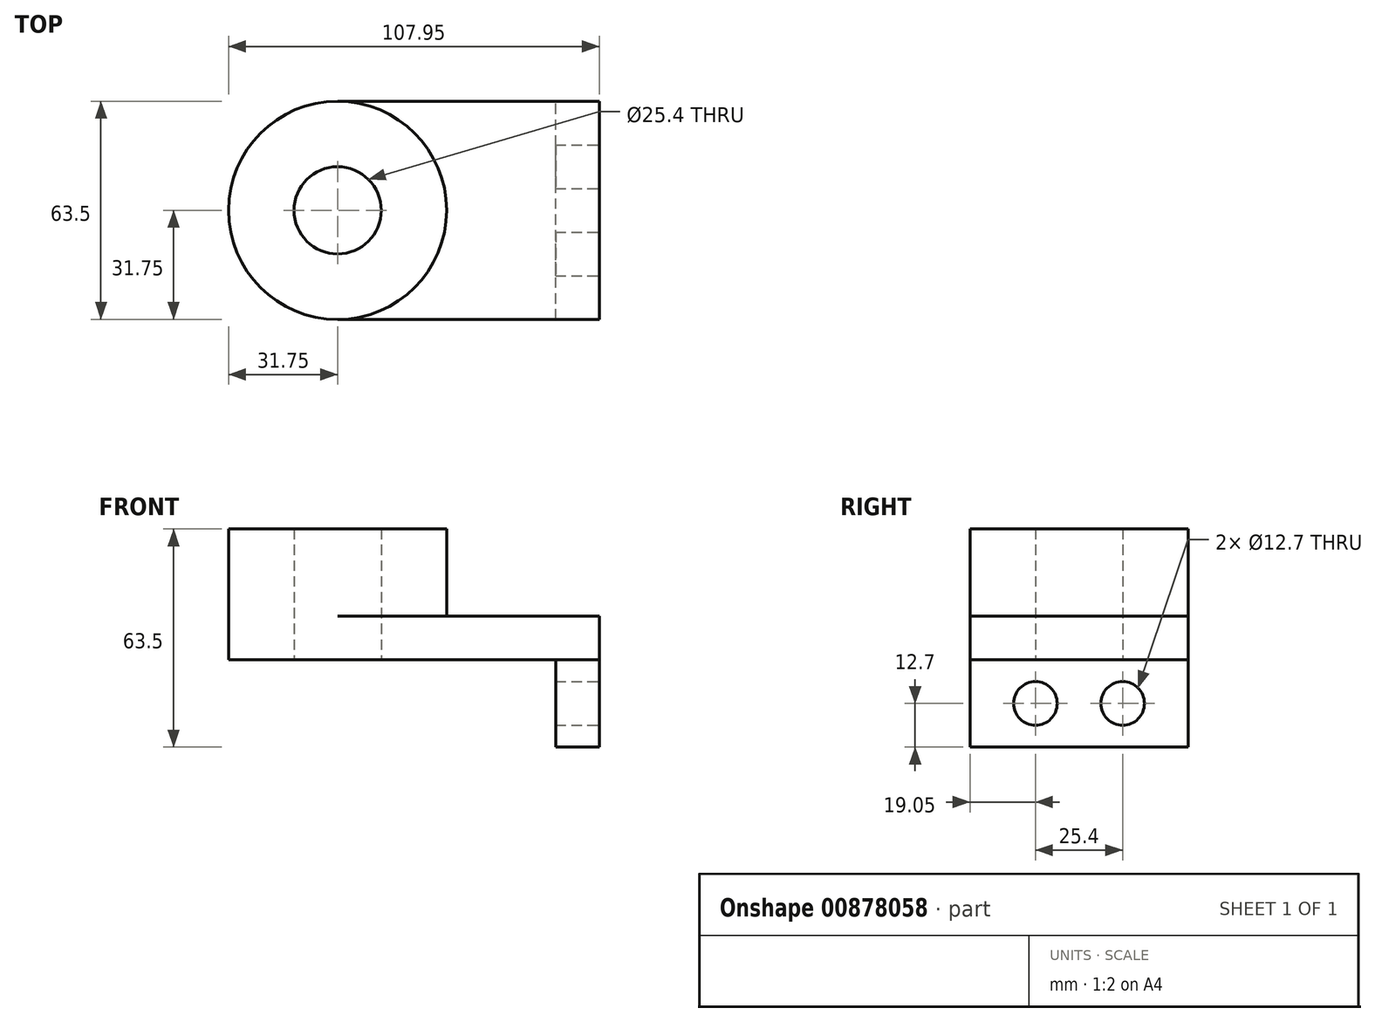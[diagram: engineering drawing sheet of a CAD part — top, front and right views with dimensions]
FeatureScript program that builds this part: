
annotation { "Feature Type Name" : "Feature", "Feature Type Description" : "" }
export const myFeature = defineFeature(function(context is Context, id is Id, definition is map)
    precondition{}
    {
        {
            var Q0;
            Q0=qCreatedBy(makeId("Top.planeOp"),FACE);
            var sketch = newSketch(context, id + "F0", { "sketchPlane" : qUnion([Q0])});
            skLineSegment(sketch, "E0.bottom", {"start": v(38.1, -31.75) * mm, "end": v(-38.1, -31.75) * mm});
            skLineSegment(sketch, "E0.top", {"start": v(38.1, 31.75) * mm, "end": v(-38.1, 31.75) * mm});
            skLineSegment(sketch, "E0.left", {"start": v(38.1, -31.75) * mm, "end": v(38.1, 31.75) * mm});
            skLineSegment(sketch, "E0.right", {"start": v(-38.1, -31.75) * mm, "end": v(-38.1, 31.75) * mm});
            skPoint(sketch, "E0.middle", {"position": v(0, 0) * mm});
            skCircle(sketch, "E1", {"center": v(-38.1, 0) * mm, "radius": 31.75 * mm});
            skCircle(sketch, "E2", {"center": v(-38.1, 0) * mm, "radius": 12.7 * mm});
            skSolve(sketch);
        }
        {
            var Q0;
            {var subQ0=sQuery(id+"F0.wireOp",EDGE,"E0.bottom");Q0=makeQuery(id+"F0.imprint","IMPRINT",FACE,{"disambiguationData":[TD([[makeQuery(id+"F0.imprint","IMPRINT",EDGE,{"derivedFrom":subQ0}),-1.0]])]});}
            var Q1;
            {var subQ1=sQuery(id+"F0.wireOp",EDGE,"E0.right");var subQ3=sQuery(id+"F0.wireOp",EDGE,"E2");var subQ4=makeQuery(id+"F0.imprint","INTERSECT",VERTEX,{"disambiguationData":[OD(0.0)],"derivedFrom":[subQ1,subQ3]});Q1=makeQuery(id+"F0.imprint","IMPRINT",FACE,{"disambiguationData":[TD([[makeQuery(id+"F0.imprint","IMPRINT",EDGE,{"disambiguationData":[TD([[subQ4,1.0]])],"derivedFrom":subQ3}),-1.0]])]});}
            var Q2;
            {var subQ1=sQuery(id+"F0.wireOp",EDGE,"E0.right");var subQ3=sQuery(id+"F0.wireOp",EDGE,"E2");var subQ4=makeQuery(id+"F0.imprint","INTERSECT",VERTEX,{"disambiguationData":[OD(0.0)],"derivedFrom":[subQ1,subQ3]});Q2=makeQuery(id+"F0.imprint","IMPRINT",FACE,{"disambiguationData":[TD([[makeQuery(id+"F0.imprint","IMPRINT",EDGE,{"disambiguationData":[TD([[subQ4,-1.0]])],"derivedFrom":subQ3}),-1.0]])]});}
            extrude(context, id + "F1", {"entities" : qUnion([Q0, Q1, Q2]), "depth" : 12.7 * mm, "offsetDistance" : 25.4 * mm});
        }
        {
            var Q0;
            {var subQ1=sQuery(id+"F0.wireOp",EDGE,"E0.right");var subQ3=sQuery(id+"F0.wireOp",EDGE,"E2");var subQ4=makeQuery(id+"F0.imprint","INTERSECT",VERTEX,{"disambiguationData":[OD(0.0)],"derivedFrom":[subQ1,subQ3]});Q0=makeQuery(id+"F0.imprint","IMPRINT",FACE,{"disambiguationData":[TD([[makeQuery(id+"F0.imprint","IMPRINT",EDGE,{"disambiguationData":[TD([[subQ4,1.0]])],"derivedFrom":subQ3}),-1.0]])]});}
            var Q1;
            {var subQ1=sQuery(id+"F0.wireOp",EDGE,"E0.right");var subQ3=sQuery(id+"F0.wireOp",EDGE,"E2");var subQ4=makeQuery(id+"F0.imprint","INTERSECT",VERTEX,{"disambiguationData":[OD(0.0)],"derivedFrom":[subQ1,subQ3]});Q1=makeQuery(id+"F0.imprint","IMPRINT",FACE,{"disambiguationData":[TD([[makeQuery(id+"F0.imprint","IMPRINT",EDGE,{"disambiguationData":[TD([[subQ4,-1.0]])],"derivedFrom":subQ3}),-1.0]])]});}
            extrude(context, id + "F2", {"entities" : qUnion([Q0, Q1]), "operationType" : NewBodyOperationType.ADD, "depth" : 38.1 * mm, "offsetDistance" : 25.4 * mm});
        }
        {
            var Q0;
            Q0=makeQuery(id+"F1.opExtrude","SWEPT_FACE",FACE,{"disambiguationData":[OSD([sQuery(id+"F0.wireOp",EDGE,"E0.left")])]});
            var sketch = newSketch(context, id + "F3", { "sketchPlane" : qUnion([Q0])});
            skLineSegment(sketch, "E3.bottom", {"start": v(-31.75, 12.7) * mm, "end": v(31.75, 12.7) * mm});
            skLineSegment(sketch, "E3.top", {"start": v(-31.75, -25.4) * mm, "end": v(31.75, -25.4) * mm});
            skLineSegment(sketch, "E3.left", {"start": v(-31.75, 12.7) * mm, "end": v(-31.75, -25.4) * mm});
            skLineSegment(sketch, "E3.right", {"start": v(31.75, 12.7) * mm, "end": v(31.75, -25.4) * mm});
            skCircle(sketch, "E4", {"center": v(-12.7, -12.7) * mm, "radius": 6.35 * mm});
            skLineSegment(sketch, "E5", {"start": v(0, 0) * mm, "end": v(0, -25.4) * mm});
            skCircle(sketch, "E6.MirrorC", {"center": v(12.7, -12.7) * mm, "radius": 6.35 * mm});
            skSolve(sketch);
        }
        {
            var Q0;
            Q0=makeQuery(id+"F3.imprint","IMPRINT",FACE,{"disambiguationData":[TD([[makeQuery(id+"F3.imprint","IMPRINT",EDGE,{"derivedFrom":sQuery(id+"F3.wireOp",EDGE,"E4")}),-1.0]])]});
            var Q1;
            {var subQ0=sQuery(id+"F3.wireOp",EDGE,"E5");Q1=makeQuery(id+"F3.imprint","IMPRINT",FACE,{"disambiguationData":[TD([[makeQuery(id+"F3.imprint","IMPRINT",EDGE,{"derivedFrom":subQ0}),1.0]])]});}
            extrude(context, id + "F4", {"entities" : qUnion([Q0, Q1]), "oppositeDirection" : true, "depth" : 12.7 * mm, "offsetDistance" : 25.4 * mm});
        }
    });
